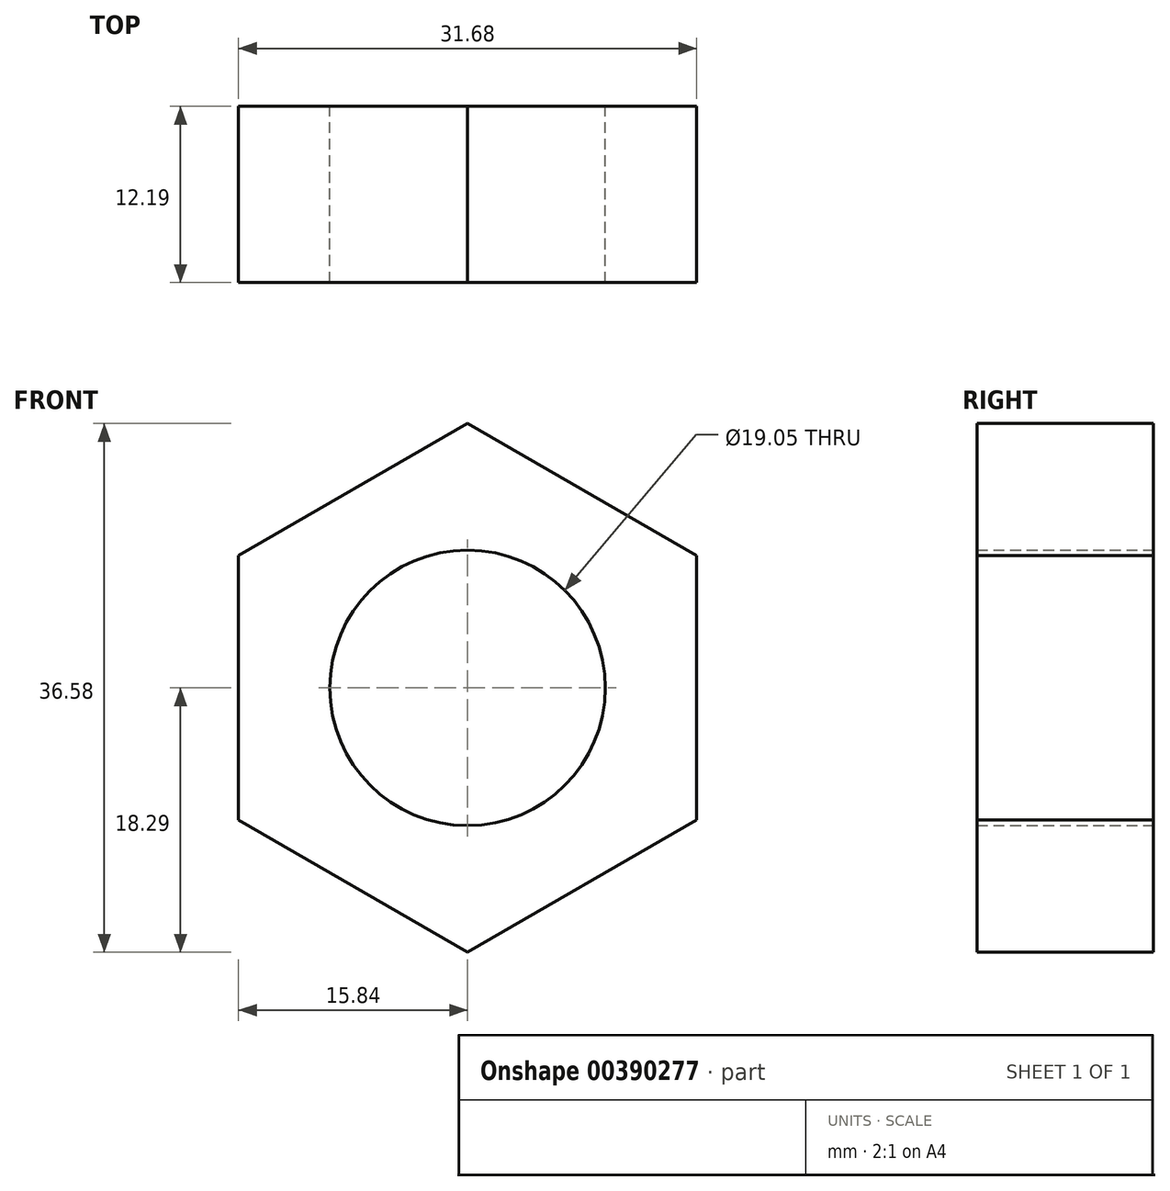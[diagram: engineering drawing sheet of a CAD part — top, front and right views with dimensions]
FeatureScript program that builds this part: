
annotation { "Feature Type Name" : "Feature", "Feature Type Description" : "" }
export const myFeature = defineFeature(function(context is Context, id is Id, definition is map)
    precondition{}
    {
        {
            var Q0;
            Q0=qCreatedBy(makeId("Front.planeOp"),FACE);
            var sketch = newSketch(context, id + "F0", { "sketchPlane" : qUnion([Q0])});
            skCircle(sketch, "E0.cCircle", {"center": v(0, 0) * mm, "radius": 15.84 * mm, "construction": true});
            skLineSegment(sketch, "E0.0", {"start": v(-15.84, -9.14) * mm, "end": v(-15.84, 9.14) * mm});
            skLineSegment(sketch, "E0.1", {"start": v(-15.84, 9.14) * mm, "end": v(0, 18.29) * mm});
            skLineSegment(sketch, "E0.2", {"start": v(0, 18.29) * mm, "end": v(15.84, 9.14) * mm});
            skLineSegment(sketch, "E0.3", {"start": v(15.84, 9.14) * mm, "end": v(15.84, -9.14) * mm});
            skLineSegment(sketch, "E0.4", {"start": v(15.84, -9.14) * mm, "end": v(0, -18.29) * mm});
            skLineSegment(sketch, "E0.5", {"start": v(0, -18.29) * mm, "end": v(-15.84, -9.14) * mm});
            skPoint(sketch, "E0.0.midPoint", {"position": v(-15.84, 0) * mm});
            skCircle(sketch, "E1", {"center": v(0, 0) * mm, "radius": 9.53 * mm});
            skSolve(sketch);
        }
        {
            var Q0;
            Q0 = qSketchRegion(id + "F0", true);
            extrude(context, id + "F1", {"entities" : qUnion([Q0]), "depth" : 12.2 * mm});
        }
    });
